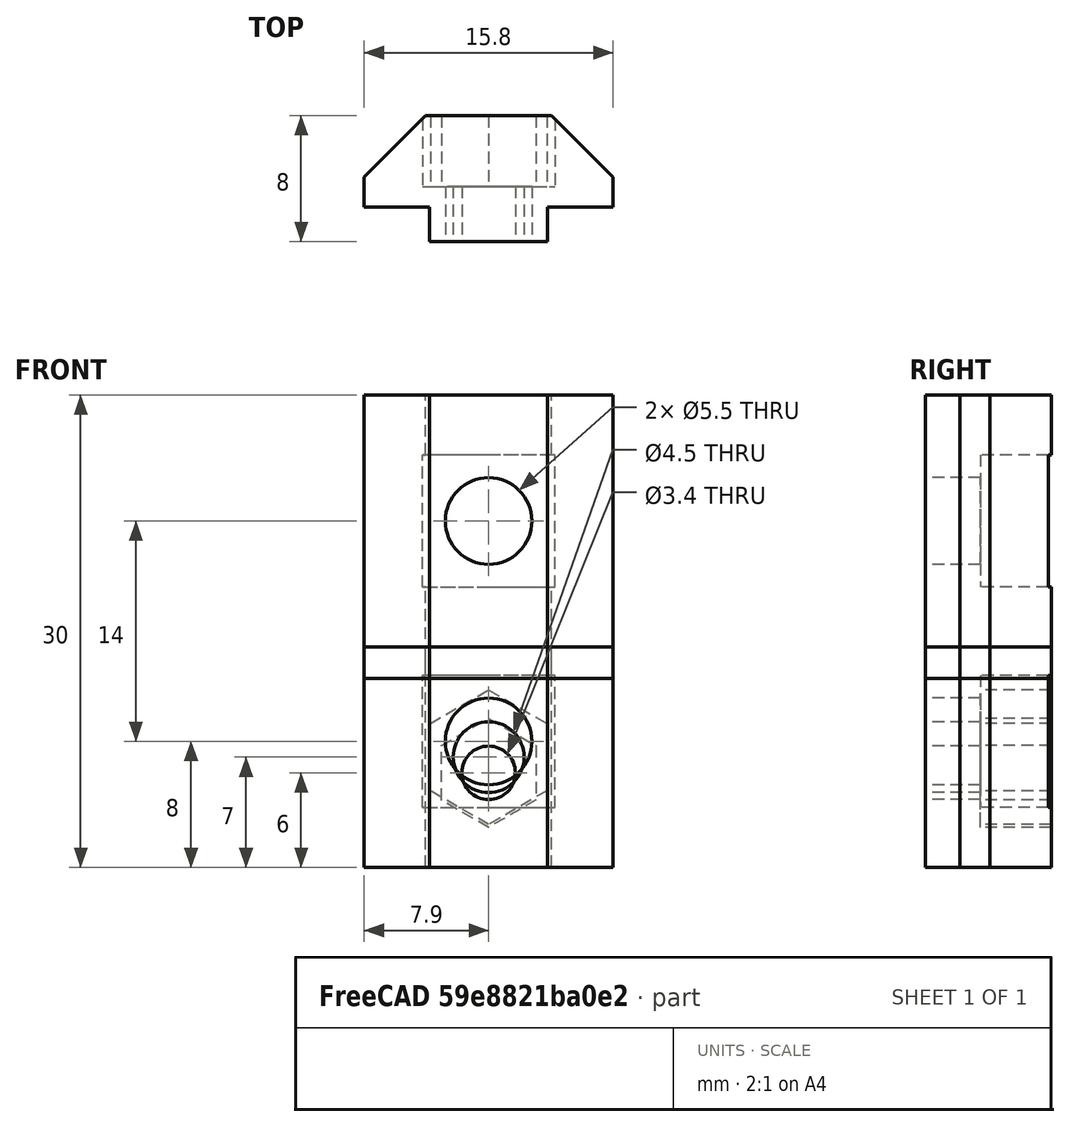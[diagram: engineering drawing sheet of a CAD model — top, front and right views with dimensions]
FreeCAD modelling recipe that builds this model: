
FCSTD DOCUMENT  (FreeCAD 0.19R24366 (Git))
Label: T_Nut-30x30
License: All rights reserved
LicenseURL: http://en.wikipedia.org/wiki/All_rights_reserved
objects: Sketcher::SketchObject×12, PartDesign::Pad×4, PartDesign::Mirrored×4, PartDesign::Plane×4, PartDesign::Pocket×4, PartDesign::LinearPattern×4, PartDesign::Hole×4, PartDesign::Body×4, App::Part×4, Mesh::Feature×4
note: 52 computed .brp shape members not serialized (recipe doc carries the construction recipe); baked Part::Feature solids carry a one-line shape summary decoded from their .brp

FEATURE [Sketcher::SketchObject] Sketch002  label="base sketch"
  FullyConstrained = true
  MapMode = 5
  Support = -> [XY_Plane004]
  sketch-geometry (7):
    g0: LineSegment StartX=0 StartY=0 StartZ=0 EndX=0 EndY=8 EndZ=0
    g1: LineSegment StartX=0 StartY=8 StartZ=0 EndX=-4 EndY=8 EndZ=0
    g2: LineSegment StartX=-4 StartY=8 StartZ=0 EndX=-7.9 EndY=4.1 EndZ=0
    g3: LineSegment StartX=-7.9 StartY=4.1 StartZ=0 EndX=-7.9 EndY=2.2 EndZ=0
    g4: LineSegment StartX=-7.9 StartY=2.2 StartZ=0 EndX=-3.75 EndY=2.2 EndZ=0
    g5: LineSegment StartX=-3.75 StartY=2.2 StartZ=0 EndX=-3.75 EndY=0 EndZ=0
    g6: LineSegment StartX=-3.75 StartY=0 StartZ=0 EndX=0 EndY=0 EndZ=0
  constraints (20):
    c: Coincident(g-1,g0)
    c: Coincident(g0,g1)
    c: Horizontal(g1)
    c: Coincident(g1,g2)
    c: Coincident(g2,g3)
    c: Vertical(g3)
    c: Coincident(g3,g4)
    c: Horizontal(g4)
    c: Coincident(g4,g5)
    c: PointOnObject(g5,g-1)
    c: Vertical(g5)
    c: Coincident(g5,g6)
    c: Coincident(g6,g0)
    c: DistanceX(g1,g0) = 4
    c: DistanceY(g3,g2) = 1.9
    c: DistanceY(g5,g4) = 2.2
    c: DistanceX(g5,g0) = 3.75
    c: Vertical(g0)
    c: DistanceY(g0,g0) = 8
    c: DistanceX(g3,g0) = 7.9
FEATURE [PartDesign::Pad] Pad002  label="base pad"
  Direction = (1,1,1)
  Length = 30
  Length2 = 100
  Profile = -> Sketch002
  Refine = true
  Type = 0
FEATURE [PartDesign::Mirrored] Mirrored  label="base pad mirrored"
  BaseFeature = -> Pad002
  MirrorPlane = -> Sketch002 [V_Axis]
  Originals = -> [Pad002]
FEATURE [PartDesign::Plane] DatumPlane
  Length = 60.4881
  MapMode = 5
  Placement = pos=(0,8,0) rot=(0,0.707107,0.707107;3.14159rad)
  ResizeMode = 0
  Support = -> [Mirrored]
  Width = 65.4881
FEATURE [Sketcher::SketchObject] Sketch  label="Hex nut sketch"
  FullyConstrained = true
  MapMode = 5
  Placement = pos=(0,8,0) rot=(0,0.707107,0.707107;3.14159rad)
  Support = -> [DatumPlane]
  sketch-geometry (7):
    g0: LineSegment StartX=0 StartY=2.72761 StartZ=0 EndX=3.7 EndY=4.8638 EndZ=0
    g1: LineSegment StartX=3.7 StartY=4.8638 StartZ=0 EndX=3.7 EndY=9.1362 EndZ=0
    g2: LineSegment StartX=3.7 StartY=9.1362 StartZ=0 EndX=1.50844e-11 EndY=11.2724 EndZ=0
    g3: LineSegment StartX=1.50844e-11 StartY=11.2724 StartZ=0 EndX=-3.7 EndY=9.1362 EndZ=0
    g4: LineSegment StartX=-3.7 StartY=9.1362 StartZ=0 EndX=-3.7 EndY=4.8638 EndZ=0
    g5: LineSegment StartX=-3.7 StartY=4.8638 StartZ=0 EndX=0 EndY=2.72761 EndZ=0
    g6: Circle CenterX=0 CenterY=7 CenterZ=0 NormalX=0 NormalY=0 NormalZ=1 AngleXU=0 Radius=4.27239
  constraints (17):
    c: Coincident(g0,g1)
    c: Coincident(g1,g2)
    c: Coincident(g2,g3)
    c: Coincident(g3,g4)
    c: Coincident(g4,g5)
    c: Coincident(g5,g0)
    c: Equal(g0, g1-g5) x5
    c: PointOnObject(g0,g6)
    c: PointOnObject(g1,g6)
    c: PointOnObject(g2,g6)
    c: PointOnObject(g3,g6)
    c: PointOnObject(g4,g6)
    c: PointOnObject(g5,g6)
    c: PointOnObject(g6,g-2)
    c: PointOnObject(g5,g-2)
    c: DistanceX(g6,g1) = 3.7
    c: DistanceY(g-1,g6) = 7
FEATURE [PartDesign::Pocket] Pocket  label="Hex nut pocket"
  BaseFeature = -> Mirrored
  Length = 4.5
  Length2 = 100
  Profile = -> Sketch
  Type = 0
FEATURE [PartDesign::LinearPattern] LinearPattern  label="Hex nut pockets pattern"
  BaseFeature = -> Pocket
  Direction = -> Sketch [V_Axis]
  Length = 16
  Occurrences = 2
  Originals = -> [Pocket]
FEATURE [Sketcher::SketchObject] Sketch003  label="M4 hole sketch"
  FullyConstrained = true
  MapMode = 5
  Placement = pos=(0,8,0) rot=(0,0.707107,0.707107;3.14159rad)
  Support = -> [DatumPlane]
  sketch-geometry (1):
    g0: Circle CenterX=0 CenterY=7.3 CenterZ=0 NormalX=0 NormalY=0 NormalZ=1 AngleXU=0 Radius=1.75
  constraints (3):
    c: PointOnObject(g0,g-2)
    c: Diameter(g0) = 3.5
    c: DistanceY(g-1,g0) = 7.3
FEATURE [PartDesign::Hole] Hole  label="M4 hole"
  BaseFeature = -> LinearPattern
  Depth = 25
  DepthType = 0
  Diameter = 4.5
  DrillForDepth = false
  DrillPoint = 1
  DrillPointAngle = 118
  HoleCutCountersinkAngle = 90
  HoleCutCustomValues = false
  HoleCutDepth = 0
  HoleCutDiameter = 6.1
  HoleCutType = 0
  ModelActualThread = false
  Profile = -> Sketch003
  Tapered = false
  TaperedAngle = 90
  ThreadAngle = 0
  ThreadClass = 0
  ThreadCutOffInner = 0
  ThreadCutOffOuter = 0
  ThreadDirection = 0
  ThreadFit = 0
  ThreadPitch = 0
  ThreadSize = 11
  ThreadType = 1
  Threaded = false
FEATURE [PartDesign::LinearPattern] LinearPattern001  label="M4 holes pattern"
  BaseFeature = -> Hole
  Direction = -> Sketch003 [V_Axis]
  Length = 16
  Occurrences = 2
  Originals = -> [Hole]
FEATURE [PartDesign::Body] Body002  label="T-nut base body"
  Group = -> [Sketch002,Pad002,Mirrored,DatumPlane,Sketch,Pocket,LinearPattern,Sketch003,Hole,LinearPattern001]
  Origin = -> Origin004
  Tip = -> LinearPattern001
FEATURE [App::Part] Part001  label="3030-T-nut-2xM4-hex"
  Group = -> [Body002]
  Origin = -> Origin003
  Placement = pos=(-18,0,0) rot=(0,0,1;0rad)
FEATURE [Sketcher::SketchObject] Sketch006  label="base sketch001"
  FullyConstrained = true
  MapMode = 5
  Support = -> [XY_Plane006]
  sketch-geometry (7):
    g0: LineSegment StartX=0 StartY=0 StartZ=0 EndX=0 EndY=8 EndZ=0
    g1: LineSegment StartX=0 StartY=8 StartZ=0 EndX=-4 EndY=8 EndZ=0
    g2: LineSegment StartX=-4 StartY=8 StartZ=0 EndX=-7.9 EndY=4.1 EndZ=0
    g3: LineSegment StartX=-7.9 StartY=4.1 StartZ=0 EndX=-7.9 EndY=2.2 EndZ=0
    g4: LineSegment StartX=-7.9 StartY=2.2 StartZ=0 EndX=-3.75 EndY=2.2 EndZ=0
    g5: LineSegment StartX=-3.75 StartY=2.2 StartZ=0 EndX=-3.75 EndY=0 EndZ=0
    g6: LineSegment StartX=-3.75 StartY=0 StartZ=0 EndX=0 EndY=0 EndZ=0
  constraints (20):
    c: Coincident(g-1,g0)
    c: Coincident(g0,g1)
    c: Horizontal(g1)
    c: Coincident(g1,g2)
    c: Coincident(g2,g3)
    c: Vertical(g3)
    c: Coincident(g3,g4)
    c: Horizontal(g4)
    c: Coincident(g4,g5)
    c: PointOnObject(g5,g-1)
    c: Vertical(g5)
    c: Coincident(g5,g6)
    c: Coincident(g6,g0)
    c: DistanceX(g1,g0) = 4
    c: DistanceY(g3,g2) = 1.9
    c: DistanceY(g5,g4) = 2.2
    c: DistanceX(g5,g0) = 3.75
    c: Vertical(g0)
    c: DistanceY(g0,g0) = 8
    c: DistanceX(g3,g0) = 7.9
FEATURE [PartDesign::Pad] Pad003  label="base pad001"
  Direction = (1,1,1)
  Length = 30
  Length2 = 100
  Profile = -> Sketch006
  Refine = true
  Type = 0
FEATURE [PartDesign::Mirrored] Mirrored001  label="base pad mirrored001"
  BaseFeature = -> Pad003
  MirrorPlane = -> Sketch006 [V_Axis]
  Originals = -> [Pad003]
FEATURE [PartDesign::Plane] DatumPlane001
  Length = 60.4881
  MapMode = 5
  Placement = pos=(0,8,0) rot=(0,0.707107,0.707107;3.14159rad)
  ResizeMode = 0
  Support = -> [Mirrored001]
  Width = 65.4881
FEATURE [Sketcher::SketchObject] Sketch005  label="Flat nut sketch001"
  FullyConstrained = true
  MapMode = 5
  Placement = pos=(0,8,0) rot=(0,0.707107,0.707107;3.14159rad)
  Support = -> [DatumPlane001]
  sketch-geometry (4):
    g0: LineSegment StartX=-4.2 StartY=12.2 StartZ=0 EndX=4.2 EndY=12.2 EndZ=0
    g1: LineSegment StartX=4.2 StartY=12.2 StartZ=0 EndX=4.2 EndY=3.8 EndZ=0
    g2: LineSegment StartX=4.2 StartY=3.8 StartZ=0 EndX=-4.2 EndY=3.8 EndZ=0
    g3: LineSegment StartX=-4.2 StartY=3.8 StartZ=0 EndX=-4.2 EndY=12.2 EndZ=0
  constraints (11):
    c: Coincident(g0,g1)
    c: Coincident(g1,g2)
    c: Coincident(g2,g3)
    c: Coincident(g3,g0)
    c: Horizontal(g0)
    c: Vertical(g1)
    c: Vertical(g3)
    c: Symmetric(g1,g2,g-2)
    c: DistanceY(g1,g0) = 8.4
    c: DistanceX(g2,g1) = 8.4
    c: DistanceY(g-1,g2) = 3.8
FEATURE [PartDesign::Pocket] Pocket001  label="Flat nut pocket"
  BaseFeature = -> Mirrored001
  Length = 4.5
  Length2 = 100
  Profile = -> Sketch005
  Type = 0
FEATURE [Sketcher::SketchObject] Sketch004  label="M4 hole sketch001"
  FullyConstrained = true
  MapMode = 5
  Placement = pos=(0,8,0) rot=(0,0.707107,0.707107;3.14159rad)
  Support = -> [DatumPlane001]
  sketch-geometry (1):
    g0: Circle CenterX=0 CenterY=8 CenterZ=0 NormalX=0 NormalY=0 NormalZ=1 AngleXU=0 Radius=1.75
  constraints (3):
    c: PointOnObject(g0,g-2)
    c: Diameter(g0) = 3.5
    c: DistanceY(g-1,g0) = 8
FEATURE [PartDesign::LinearPattern] LinearPattern002  label="Flat nut pockets pattern"
  BaseFeature = -> Pocket001
  Direction = -> Sketch005 [V_Axis]
  Length = 14
  Occurrences = 2
  Originals = -> [Pocket001]
FEATURE [PartDesign::Hole] Hole001  label="M5 hole"
  BaseFeature = -> LinearPattern002
  Depth = 25
  DepthType = 0
  Diameter = 5.5
  DrillForDepth = false
  DrillPoint = 1
  DrillPointAngle = 118
  HoleCutCountersinkAngle = 90
  HoleCutCustomValues = false
  HoleCutDepth = 0
  HoleCutDiameter = 6.1
  HoleCutType = 0
  ModelActualThread = false
  Profile = -> Sketch004
  Tapered = false
  TaperedAngle = 90
  ThreadAngle = 0
  ThreadClass = 0
  ThreadCutOffInner = 0
  ThreadCutOffOuter = 0
  ThreadDirection = 0
  ThreadFit = 0
  ThreadPitch = 0
  ThreadSize = 13
  ThreadType = 1
  Threaded = false
FEATURE [PartDesign::LinearPattern] LinearPattern003  label="M5 holes pattern"
  BaseFeature = -> Hole001
  Direction = -> Sketch004 [V_Axis]
  Length = 14
  Occurrences = 2
  Originals = -> [Hole001]
FEATURE [PartDesign::Body] Body002003  label="T-nut base body003"
  Group = -> [Sketch006,Pad003,Mirrored001,DatumPlane001,Sketch005,Pocket001,LinearPattern002,Sketch004,Hole001,LinearPattern003]
  Origin = -> Origin005
  Tip = -> LinearPattern003
FEATURE [App::Part] Part002  label="3030-T-nut-2xM5-flat"
  Group = -> [Body002003]
  Origin = -> Origin006
  Placement = pos=(-36,0,0) rot=(0,0,1;0rad)
FEATURE [Sketcher::SketchObject] Sketch009  label="base sketch002"
  FullyConstrained = true
  MapMode = 5
  Support = -> [XY_Plane007]
  sketch-geometry (7):
    g0: LineSegment StartX=0 StartY=0 StartZ=0 EndX=0 EndY=8 EndZ=0
    g1: LineSegment StartX=0 StartY=8 StartZ=0 EndX=-4 EndY=8 EndZ=0
    g2: LineSegment StartX=-4 StartY=8 StartZ=0 EndX=-7.9 EndY=4.1 EndZ=0
    g3: LineSegment StartX=-7.9 StartY=4.1 StartZ=0 EndX=-7.9 EndY=2.2 EndZ=0
    g4: LineSegment StartX=-7.9 StartY=2.2 StartZ=0 EndX=-3.75 EndY=2.2 EndZ=0
    g5: LineSegment StartX=-3.75 StartY=2.2 StartZ=0 EndX=-3.75 EndY=0 EndZ=0
    g6: LineSegment StartX=-3.75 StartY=0 StartZ=0 EndX=0 EndY=0 EndZ=0
  constraints (20):
    c: Coincident(g-1,g0)
    c: Coincident(g0,g1)
    c: Horizontal(g1)
    c: Coincident(g1,g2)
    c: Coincident(g2,g3)
    c: Vertical(g3)
    c: Coincident(g3,g4)
    c: Horizontal(g4)
    c: Coincident(g4,g5)
    c: PointOnObject(g5,g-1)
    c: Vertical(g5)
    c: Coincident(g5,g6)
    c: Coincident(g6,g0)
    c: DistanceX(g1,g0) = 4
    c: DistanceY(g3,g2) = 1.9
    c: DistanceY(g5,g4) = 2.2
    c: DistanceX(g5,g0) = 3.75
    c: Vertical(g0)
    c: DistanceY(g0,g0) = 8
    c: DistanceX(g3,g0) = 7.9
FEATURE [PartDesign::Pad] Pad004  label="base pad002"
  Direction = (1,1,1)
  Length = 14
  Length2 = 100
  Profile = -> Sketch009
  Refine = true
  Type = 0
FEATURE [PartDesign::Mirrored] Mirrored002  label="base pad mirrored002"
  BaseFeature = -> Pad004
  MirrorPlane = -> Sketch009 [V_Axis]
  Originals = -> [Pad004]
FEATURE [PartDesign::Plane] DatumPlane002
  Length = 60
  MapMode = 5
  Placement = pos=(0,8,0) rot=(0,0.707107,0.707107;3.14159rad)
  ResizeMode = 0
  Support = -> [Mirrored002]
  Width = 60
FEATURE [Sketcher::SketchObject] Sketch007  label="M4 hole sketch002"
  FullyConstrained = true
  MapMode = 5
  Placement = pos=(0,8,0) rot=(0,0.707107,0.707107;3.14159rad)
  Support = -> [DatumPlane002]
  sketch-geometry (1):
    g0: Circle CenterX=0 CenterY=7 CenterZ=0 NormalX=0 NormalY=0 NormalZ=1 AngleXU=0 Radius=1.75
  constraints (3):
    c: PointOnObject(g0,g-2)
    c: Diameter(g0) = 3.5
    c: DistanceY(g-1,g0) = 7
FEATURE [Sketcher::SketchObject] Sketch008  label="Hex nut sketch001"
  FullyConstrained = true
  MapMode = 5
  Placement = pos=(0,8,0) rot=(0,0.707107,0.707107;3.14159rad)
  Support = -> [DatumPlane002]
  sketch-geometry (7):
    g0: LineSegment StartX=0 StartY=2.72761 StartZ=0 EndX=3.7 EndY=4.8638 EndZ=0
    g1: LineSegment StartX=3.7 StartY=4.8638 StartZ=0 EndX=3.7 EndY=9.1362 EndZ=0
    g2: LineSegment StartX=3.7 StartY=9.1362 StartZ=0 EndX=5.906e-13 EndY=11.2724 EndZ=0
    g3: LineSegment StartX=5.906e-13 StartY=11.2724 StartZ=0 EndX=-3.7 EndY=9.1362 EndZ=0
    g4: LineSegment StartX=-3.7 StartY=9.1362 StartZ=0 EndX=-3.7 EndY=4.8638 EndZ=0
    g5: LineSegment StartX=-3.7 StartY=4.8638 StartZ=0 EndX=0 EndY=2.72761 EndZ=0
    g6: Circle CenterX=0 CenterY=7 CenterZ=0 NormalX=0 NormalY=0 NormalZ=1 AngleXU=0 Radius=4.27239
  constraints (17):
    c: Coincident(g0,g1)
    c: Coincident(g1,g2)
    c: Coincident(g2,g3)
    c: Coincident(g3,g4)
    c: Coincident(g4,g5)
    c: Coincident(g5,g0)
    c: Equal(g0, g1-g5) x5
    c: PointOnObject(g0,g6)
    c: PointOnObject(g1,g6)
    c: PointOnObject(g2,g6)
    c: PointOnObject(g3,g6)
    c: PointOnObject(g4,g6)
    c: PointOnObject(g5,g6)
    c: PointOnObject(g6,g-2)
    c: PointOnObject(g5,g-2)
    c: DistanceX(g6,g1) = 3.7
    c: DistanceY(g-1,g6) = 7
FEATURE [PartDesign::Pocket] Pocket002  label="Hex nut pocket001"
  BaseFeature = -> Mirrored002
  Length = 4.5
  Length2 = 100
  Profile = -> Sketch008
  Type = 0
FEATURE [PartDesign::Hole] Hole002  label="M4 hole001"
  BaseFeature = -> Pocket002
  Depth = 25
  DepthType = 0
  Diameter = 4.5
  DrillForDepth = false
  DrillPoint = 1
  DrillPointAngle = 118
  HoleCutCountersinkAngle = 90
  HoleCutCustomValues = false
  HoleCutDepth = 0
  HoleCutDiameter = 6.1
  HoleCutType = 0
  ModelActualThread = false
  Profile = -> Sketch007
  Tapered = false
  TaperedAngle = 90
  ThreadAngle = 0
  ThreadClass = 0
  ThreadCutOffInner = 0
  ThreadCutOffOuter = 0
  ThreadDirection = 0
  ThreadFit = 0
  ThreadPitch = 0
  ThreadSize = 11
  ThreadType = 1
  Threaded = false
FEATURE [PartDesign::Body] Body002004  label="T-nut base body004"
  Group = -> [Sketch009,Pad004,Mirrored002,DatumPlane002,Sketch008,Pocket002,Sketch007,Hole002]
  Origin = -> Origin007
  Tip = -> Hole002
FEATURE [App::Part] Part003  label="3030-T-nut-M4-hex"
  Group = -> [Body002004]
  Origin = -> Origin008
FEATURE [Sketcher::SketchObject] Sketch010  label="base sketch003"
  FullyConstrained = true
  MapMode = 5
  Support = -> [XY_Plane009]
  sketch-geometry (7):
    g0: LineSegment StartX=0 StartY=0 StartZ=0 EndX=0 EndY=8 EndZ=0
    g1: LineSegment StartX=0 StartY=8 StartZ=0 EndX=-4 EndY=8 EndZ=0
    g2: LineSegment StartX=-4 StartY=8 StartZ=0 EndX=-7.9 EndY=4.1 EndZ=0
    g3: LineSegment StartX=-7.9 StartY=4.1 StartZ=0 EndX=-7.9 EndY=2.2 EndZ=0
    g4: LineSegment StartX=-7.9 StartY=2.2 StartZ=0 EndX=-3.75 EndY=2.2 EndZ=0
    g5: LineSegment StartX=-3.75 StartY=2.2 StartZ=0 EndX=-3.75 EndY=0 EndZ=0
    g6: LineSegment StartX=-3.75 StartY=0 StartZ=0 EndX=0 EndY=0 EndZ=0
  constraints (20):
    c: Coincident(g-1,g0)
    c: Coincident(g0,g1)
    c: Horizontal(g1)
    c: Coincident(g1,g2)
    c: Coincident(g2,g3)
    c: Vertical(g3)
    c: Coincident(g3,g4)
    c: Horizontal(g4)
    c: Coincident(g4,g5)
    c: PointOnObject(g5,g-1)
    c: Vertical(g5)
    c: Coincident(g5,g6)
    c: Coincident(g6,g0)
    c: DistanceX(g1,g0) = 4
    c: DistanceY(g3,g2) = 1.9
    c: DistanceY(g5,g4) = 2.2
    c: DistanceX(g5,g0) = 3.75
    c: Vertical(g0)
    c: DistanceY(g0,g0) = 8
    c: DistanceX(g3,g0) = 7.9
FEATURE [PartDesign::Pad] Pad005  label="base pad003"
  Direction = (1,1,1)
  Length = 12
  Length2 = 100
  Profile = -> Sketch010
  Refine = true
  Type = 0
FEATURE [PartDesign::Mirrored] Mirrored003  label="base pad mirrored003"
  BaseFeature = -> Pad005
  MirrorPlane = -> Sketch010 [V_Axis]
  Originals = -> [Pad005]
FEATURE [PartDesign::Plane] DatumPlane003
  Length = 60
  MapMode = 5
  Placement = pos=(0,8,0) rot=(0,0.707107,0.707107;3.14159rad)
  ResizeMode = 0
  Support = -> [Mirrored003]
  Width = 60
FEATURE [Sketcher::SketchObject] Sketch011  label="Hex nut sketch002"
  FullyConstrained = true
  MapMode = 5
  Placement = pos=(0,8,0) rot=(0,0.707107,0.707107;3.14159rad)
  Support = -> [DatumPlane003]
  sketch-geometry (7):
    g0: LineSegment StartX=0 StartY=2.5359 StartZ=0 EndX=3 EndY=4.26795 EndZ=0
    g1: LineSegment StartX=3 StartY=4.26795 StartZ=0 EndX=3 EndY=7.73205 EndZ=0
    g2: LineSegment StartX=3 StartY=7.73205 StartZ=0 EndX=1.47e-14 EndY=9.4641 EndZ=0
    g3: LineSegment StartX=1.47e-14 StartY=9.4641 StartZ=0 EndX=-3 EndY=7.73205 EndZ=0
    g4: LineSegment StartX=-3 StartY=7.73205 StartZ=0 EndX=-3 EndY=4.26795 EndZ=0
    g5: LineSegment StartX=-3 StartY=4.26795 StartZ=0 EndX=0 EndY=2.5359 EndZ=0
    g6: Circle CenterX=0 CenterY=6 CenterZ=0 NormalX=0 NormalY=0 NormalZ=1 AngleXU=0 Radius=3.4641
  constraints (17):
    c: Coincident(g0,g1)
    c: Coincident(g1,g2)
    c: Coincident(g2,g3)
    c: Coincident(g3,g4)
    c: Coincident(g4,g5)
    c: Coincident(g5,g0)
    c: Equal(g0, g1-g5) x5
    c: PointOnObject(g0,g6)
    c: PointOnObject(g1,g6)
    c: PointOnObject(g2,g6)
    c: PointOnObject(g3,g6)
    c: PointOnObject(g4,g6)
    c: PointOnObject(g5,g6)
    c: PointOnObject(g6,g-2)
    c: PointOnObject(g5,g-2)
    c: DistanceX(g6,g1) = 3
    c: DistanceY(g-1,g6) = 6
FEATURE [Sketcher::SketchObject] Sketch012  label="M4 hole sketch003"
  FullyConstrained = true
  MapMode = 5
  Placement = pos=(0,8,0) rot=(0,0.707107,0.707107;3.14159rad)
  Support = -> [DatumPlane003]
  sketch-geometry (1):
    g0: Circle CenterX=0 CenterY=6 CenterZ=0 NormalX=0 NormalY=0 NormalZ=1 AngleXU=0 Radius=1.75
  constraints (3):
    c: PointOnObject(g0,g-2)
    c: Diameter(g0) = 3.5
    c: DistanceY(g-1,g0) = 6
FEATURE [PartDesign::Pocket] Pocket003  label="Hex nut pocket002"
  BaseFeature = -> Mirrored003
  Length = 4.5
  Length2 = 100
  Profile = -> Sketch011
  Type = 0
FEATURE [PartDesign::Hole] Hole003  label="M3 hole"
  BaseFeature = -> Pocket003
  Depth = 25
  DepthType = 0
  Diameter = 3.4
  DrillForDepth = false
  DrillPoint = 1
  DrillPointAngle = 118
  HoleCutCountersinkAngle = 90
  HoleCutCustomValues = false
  HoleCutDepth = 0
  HoleCutDiameter = 6.1
  HoleCutType = 0
  ModelActualThread = false
  Profile = -> Sketch012
  Tapered = false
  TaperedAngle = 90
  ThreadAngle = 0
  ThreadClass = 0
  ThreadCutOffInner = 0
  ThreadCutOffOuter = 0
  ThreadDirection = 0
  ThreadFit = 0
  ThreadPitch = 0
  ThreadSize = 9
  ThreadType = 1
  Threaded = false
FEATURE [PartDesign::Body] Body002005  label="T-nut base body005"
  Group = -> [Sketch010,Pad005,Mirrored003,DatumPlane003,Sketch011,Pocket003,Sketch012,Hole003]
  Origin = -> Origin009
  Tip = -> Hole003
FEATURE [App::Part] Part004  label="3030-T-nut-M3-hex"
  Group = -> [Body002005]
  Origin = -> Origin010
  Placement = pos=(18,0,0) rot=(0,0,1;0rad)
FEATURE [Mesh::Feature] Mesh  label="3030-T-nut-M3-hex (Meshed)"
FEATURE [Mesh::Feature] Mesh001  label="3030-T-nut-M4-hex (Meshed)"
FEATURE [Mesh::Feature] Mesh002  label="3030-T-nut-2xM4-hex (Meshed)"
FEATURE [Mesh::Feature] Mesh003  label="3030-T-nut-2xM5-flat (Meshed)"
